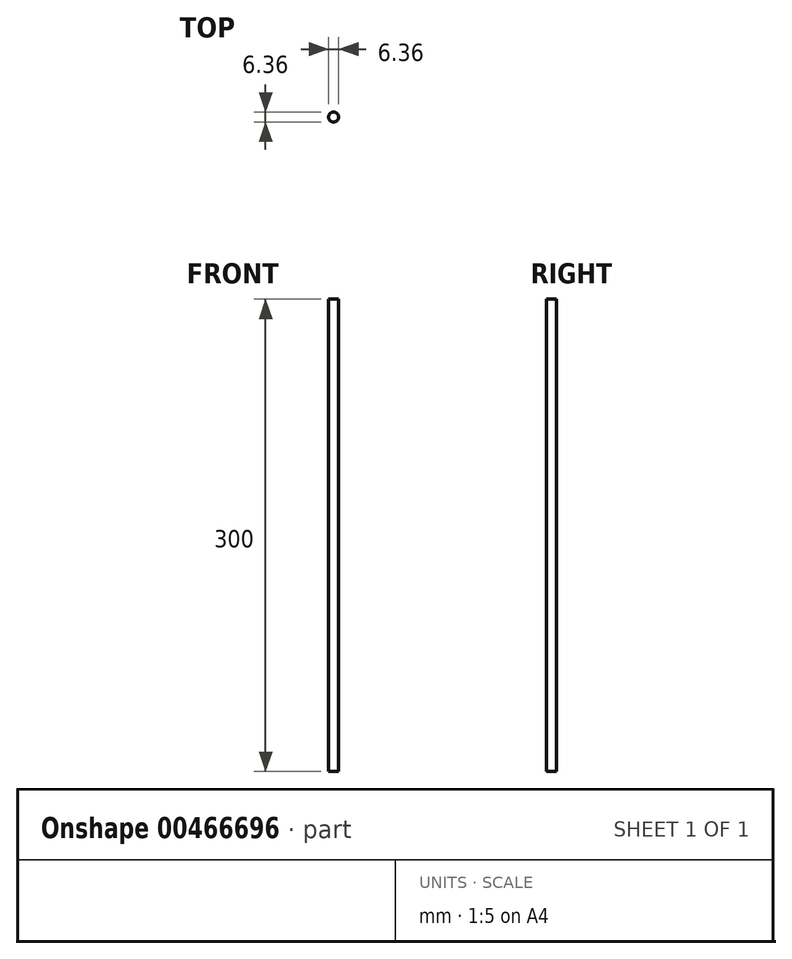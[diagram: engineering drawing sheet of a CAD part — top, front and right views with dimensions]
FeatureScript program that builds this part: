
annotation { "Feature Type Name" : "Feature", "Feature Type Description" : "" }
export const myFeature = defineFeature(function(context is Context, id is Id, definition is map)
    precondition{}
    {
        {
            var Q0;
            Q0=qCreatedBy(makeId("Top.planeOp"),FACE);
            var sketch = newSketch(context, id + "F0", { "sketchPlane" : qUnion([Q0])});
            skCircle(sketch, "E0", {"center": v(0, 0) * mm, "radius": 3.18 * mm});
            skSolve(sketch);
        }
        {
            var Q0;
            Q0 = qSketchRegion(id + "F0", true);
            extrude(context, id + "F1", {"entities" : qUnion([Q0]), "depth" : 300 * mm});
        }
    });
